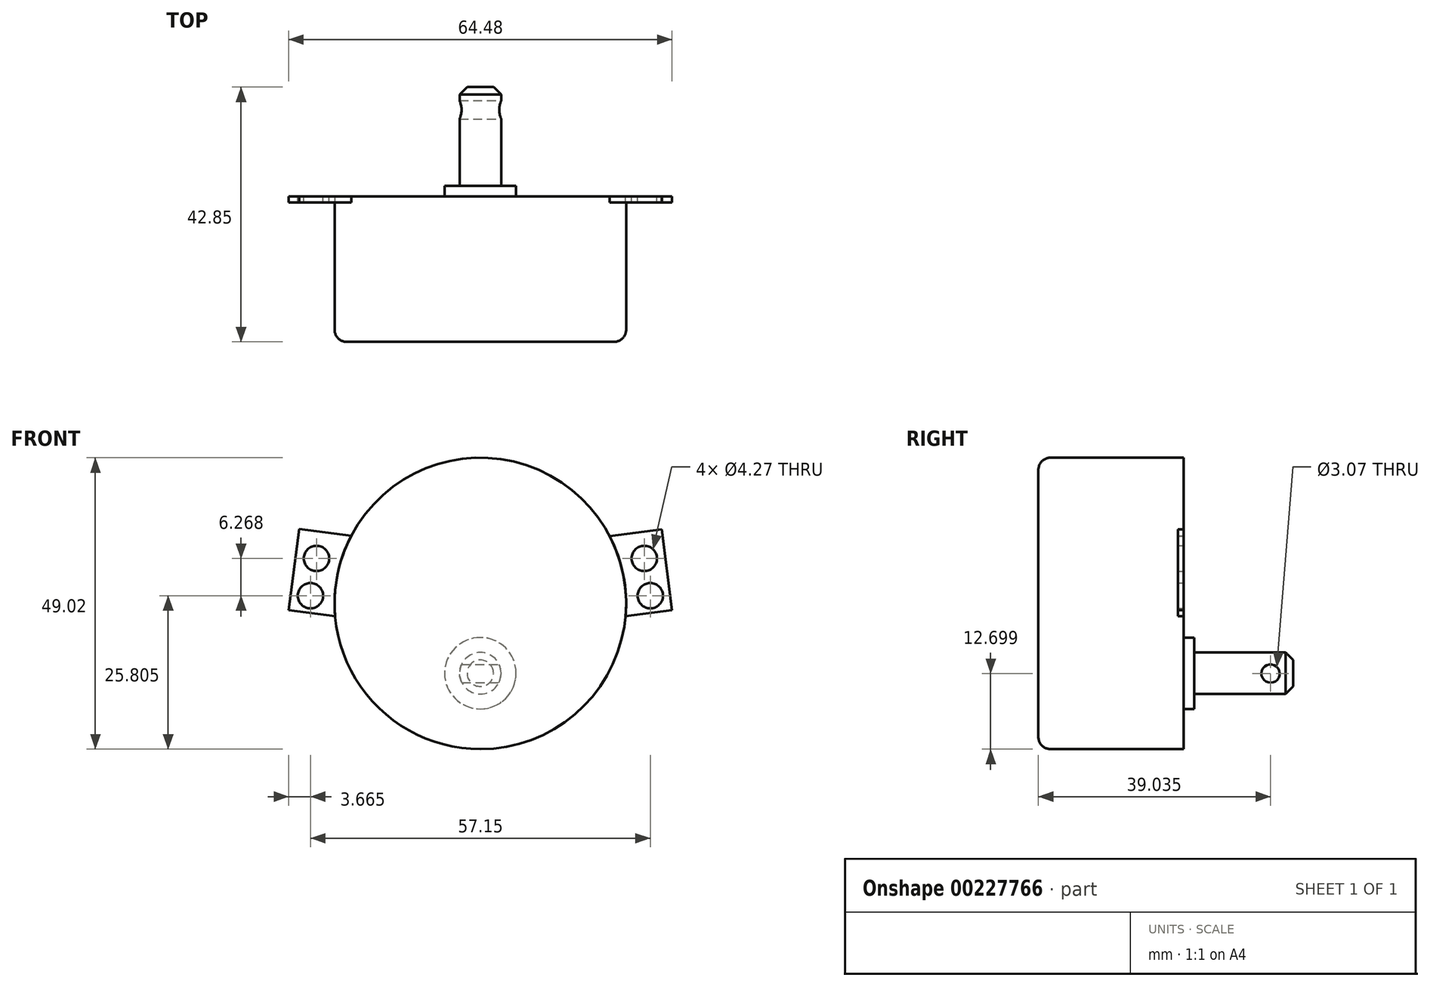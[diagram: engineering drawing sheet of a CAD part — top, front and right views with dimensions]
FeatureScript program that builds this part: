
annotation { "Feature Type Name" : "Feature", "Feature Type Description" : "" }
export const myFeature = defineFeature(function(context is Context, id is Id, definition is map)
    precondition{}
    {
        {
            var Q0;
            Q0=qCreatedBy(makeId("Front.planeOp"),FACE);
            var sketch = newSketch(context, id + "F0", { "sketchPlane" : qUnion([Q0])});
            skCircle(sketch, "E0", {"center": v(0, 0) * mm, "radius": 24.51 * mm});
            skSolve(sketch);
        }
        {
            var Q0;
            Q0 = qSketchRegion(id + "F0", true);
            extrude(context, id + "F1", {"entities" : qUnion([Q0]), "depth" : 24.43 * mm});
        }
        {
            var Q0;
            Q0=makeQuery(id+"FURY8Rx6RKXIMMn_1.boolean.opBoolean","MERGE",FACE,{"derivedFrom":[makeQuery(id+"F1.opExtrude","CAP_FACE",FACE,{"disambiguationData":[OSD([sQuery(id+"F0.wireOp",EDGE,"E0")])],"isStart":true}),makeQuery(id+"FURY8Rx6RKXIMMn_1.opExtrude","CAP_FACE",FACE,{"disambiguationData":[OSD([sQuery(id+"FCxQhorjlvF6zzP_1.wireOp",EDGE,"hhKUSKlb-nZ0b-hflR-LNPY-72FUsJaNQTWK.bottom"),sQuery(id+"FCxQhorjlvF6zzP_1.wireOp",EDGE,"hhKUSKlb-nZ0b-hflR-LNPY-72FUsJaNQTWK.top"),sQuery(id+"FCxQhorjlvF6zzP_1.wireOp",EDGE,"hhKUSKlb-nZ0b-hflR-LNPY-72FUsJaNQTWK.left"),sQuery(id+"FCxQhorjlvF6zzP_1.wireOp",EDGE,"hhKUSKlb-nZ0b-hflR-LNPY-72FUsJaNQTWK.right")])],"isStart":true})]});
            var sketch = newSketch(context, id + "F2", { "sketchPlane" : qUnion([Q0])});
            skCircle(sketch, "E1", {"center": v(0, -11.75) * mm, "radius": 3.5 * mm});
            skSolve(sketch);
        }
        {
            var Q0;
            Q0 = qSketchRegion(id + "F2", true);
            extrude(context, id + "F3", {"entities" : qUnion([Q0]), "operationType" : NewBodyOperationType.ADD, "depth" : 18.41 * mm});
        }
        {
            var Q0;
            Q0=makeQuery(id+"FURY8Rx6RKXIMMn_1.boolean.opBoolean","MERGE",FACE,{"derivedFrom":[makeQuery(id+"F1.opExtrude","CAP_FACE",FACE,{"disambiguationData":[OSD([sQuery(id+"F0.wireOp",EDGE,"E0")])],"isStart":true}),makeQuery(id+"FURY8Rx6RKXIMMn_1.opExtrude","CAP_FACE",FACE,{"disambiguationData":[OSD([sQuery(id+"FCxQhorjlvF6zzP_1.wireOp",EDGE,"hhKUSKlb-nZ0b-hflR-LNPY-72FUsJaNQTWK.bottom"),sQuery(id+"FCxQhorjlvF6zzP_1.wireOp",EDGE,"hhKUSKlb-nZ0b-hflR-LNPY-72FUsJaNQTWK.top"),sQuery(id+"FCxQhorjlvF6zzP_1.wireOp",EDGE,"hhKUSKlb-nZ0b-hflR-LNPY-72FUsJaNQTWK.left"),sQuery(id+"FCxQhorjlvF6zzP_1.wireOp",EDGE,"hhKUSKlb-nZ0b-hflR-LNPY-72FUsJaNQTWK.right")])],"isStart":true})]});
            var sketch = newSketch(context, id + "F4", { "sketchPlane" : qUnion([Q0])});
            skCircle(sketch, "E2", {"center": v(0, -11.75) * mm, "radius": 6 * mm});
            skSolve(sketch);
        }
        {
            var Q0;
            Q0 = qSketchRegion(id + "F4", true);
            extrude(context, id + "F5", {"entities" : qUnion([Q0]), "operationType" : NewBodyOperationType.ADD, "depth" : 1.78 * mm});
        }
        {
            var Q0;
            Q0=makeQuery(id+"F3.opExtrude","CAP_EDGE",EDGE,{"disambiguationData":[OSD([sQuery(id+"F2.wireOp",EDGE,"E1")])],"isStart":false});
            chamfer(context, id + "F6", {"entities" : qUnion([Q0]), "width" : 1.27 * mm, "tangentPropagation" : true});
        }
        {
            var Q0;
            Q0=qCreatedBy(makeId("Right.planeOp"),FACE);
            var sketch = newSketch(context, id + "F7", { "sketchPlane" : qUnion([Q0])});
            skCircle(sketch, "E3", {"center": v(14.6, -11.81) * mm, "radius": 1.54 * mm});
            skSolve(sketch);
        }
        {
            var Q0;
            Q0 = qSketchRegion(id + "F7", true);
            extrude(context, id + "F8", {"entities" : qUnion([Q0]), "operationType" : NewBodyOperationType.REMOVE, "oppositeDirection" : true, "depth" : 25.4 * mm, "symmetric" : true});
        }
        {
            var Q0;
            Q0=makeQuery(id+"F1.opExtrude","CAP_FACE",FACE,{"disambiguationData":[OSD([sQuery(id+"F0.wireOp",EDGE,"E0")])],"isStart":true});
            var sketch = newSketch(context, id + "F9", { "sketchPlane" : qUnion([Q0])});
            skArc(sketch, "E4", {"start": v(-21.74, 11.31) * mm, "mid": v(0.03, -24.51) * mm, "end": v(21.72, 11.36) * mm});
            skPoint(sketch, "E5.end.orphan", {"position": v(0, 9.36) * mm});
            skCircle(sketch, "E6", {"center": v(-28.58, 1.3) * mm, "radius": 2.13 * mm});
            skLineSegment(sketch, "E7", {"start": v(-24.41, -2.17) * mm, "end": v(-32.24, -1.16) * mm});
            skLineSegment(sketch, "E8", {"start": v(24.41, -2.17) * mm, "end": v(32.24, -1.16) * mm});
            skLineSegment(sketch, "E9", {"start": v(-32.24, -1.16) * mm, "end": v(-30.48, 12.44) * mm});
            skLineSegment(sketch, "E10", {"start": v(-30.48, 12.44) * mm, "end": v(-21.74, 11.31) * mm});
            skLineSegment(sketch, "E11", {"start": v(32.24, -1.16) * mm, "end": v(30.47, 12.5) * mm});
            skLineSegment(sketch, "E12", {"start": v(30.47, 12.5) * mm, "end": v(21.72, 11.36) * mm});
            skCircle(sketch, "E13", {"center": v(-27.56, 7.56) * mm, "radius": 2.13 * mm});
            skCircle(sketch, "E14", {"center": v(28.58, 1.3) * mm, "radius": 2.13 * mm});
            skCircle(sketch, "E15", {"center": v(27.56, 7.56) * mm, "radius": 2.13 * mm});
            skPoint(sketch, "E16.end.orphan", {"position": v(0, -5.33) * mm});
            skPoint(sketch, "E17.orphan", {"position": v(0, 1.3) * mm});
            skSolve(sketch);
        }
        {
            var Q0;
            Q0 = qSketchRegion(id + "F9", true);
            extrude(context, id + "F10", {"entities" : qUnion([Q0]), "operationType" : NewBodyOperationType.ADD, "oppositeDirection" : true, "depth" : 0.97 * mm});
        }
        {
            var Q0;
            Q0=makeQuery(id+"F1.opExtrude","CAP_EDGE",EDGE,{"disambiguationData":[OSD([sQuery(id+"F0.wireOp",EDGE,"E0")])],"isStart":false});
            fillet(context, id + "F11", {"entities" : qUnion([Q0]), "radius" : 2.03 * mm, "tangentPropagation" : true, "allowEdgeOverflow" : false});
        }
    });
